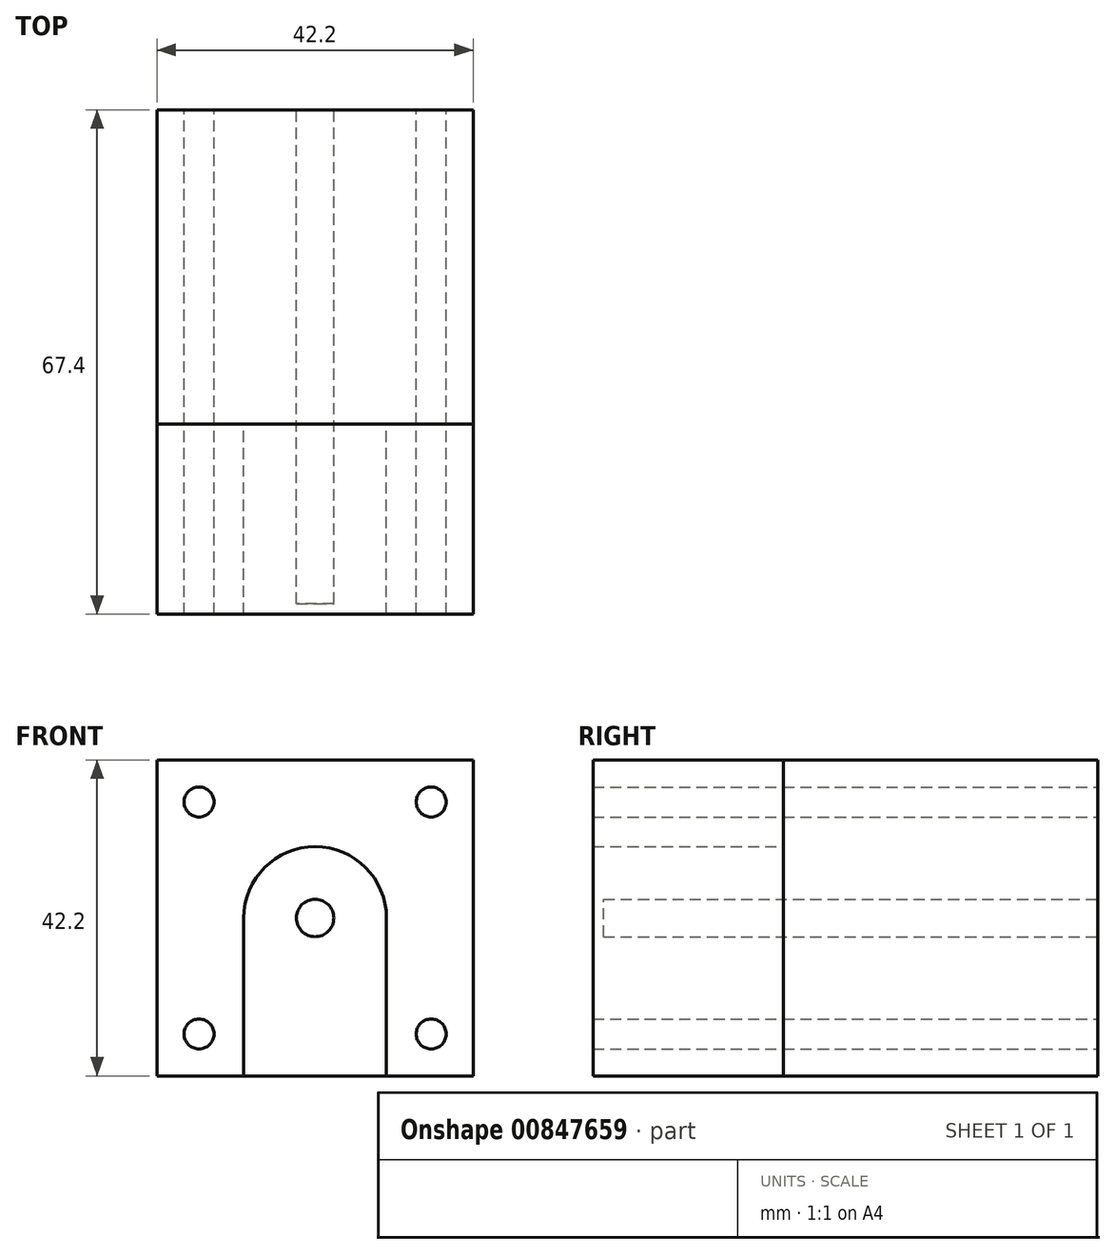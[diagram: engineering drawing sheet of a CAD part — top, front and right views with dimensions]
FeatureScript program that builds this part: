
annotation { "Feature Type Name" : "Feature", "Feature Type Description" : "" }
export const myFeature = defineFeature(function(context is Context, id is Id, definition is map)
    precondition{}
    {
        {
            var Q0;
            Q0=qCreatedBy(makeId("Front.planeOp"),FACE);
            var sketch = newSketch(context, id + "F0", { "sketchPlane" : qUnion([Q0])});
            skCircle(sketch, "E0", {"center": v(0, 0) * mm, "radius": 2.5 * mm});
            skCircle(sketch, "E1", {"center": v(0, 0) * mm, "radius": 11 * mm, "construction": true});
            skLineSegment(sketch, "E2.bottom", {"start": v(21.1, -21.1) * mm, "end": v(-21.1, -21.1) * mm});
            skLineSegment(sketch, "E2.top", {"start": v(21.1, 21.1) * mm, "end": v(-21.1, 21.1) * mm});
            skLineSegment(sketch, "E2.left", {"start": v(21.1, -21.1) * mm, "end": v(21.1, 21.1) * mm});
            skLineSegment(sketch, "E2.right", {"start": v(-21.1, -21.1) * mm, "end": v(-21.1, 21.1) * mm});
            skCircle(sketch, "E3", {"center": v(-15.5, 15.5) * mm, "radius": 2 * mm});
            skLineSegment(sketch, "E4", {"start": v(0, 21.1) * mm, "end": v(0, -21.1) * mm, "construction": true});
            skLineSegment(sketch, "E5", {"start": v(-21.1, 0) * mm, "end": v(21.1, 0) * mm, "construction": true});
            skCircle(sketch, "E6", {"center": v(15.5, 15.5) * mm, "radius": 2 * mm});
            skCircle(sketch, "E7", {"center": v(15.5, -15.5) * mm, "radius": 2 * mm});
            skCircle(sketch, "E8", {"center": v(-15.5, -15.5) * mm, "radius": 2 * mm});
            skSolve(sketch);
        }
        {
            var Q0;
            Q0=makeQuery(id+"F0.imprint","IMPRINT",FACE,{"disambiguationData":[TD([[makeQuery(id+"F0.imprint","IMPRINT",EDGE,{"derivedFrom":sQuery(id+"F0.wireOp",EDGE,"E0")}),-1.0]])]});
            var Q1;
            Q1=makeQuery(id+"F0.imprint","IMPRINT",FACE,{"disambiguationData":[TD([[makeQuery(id+"F0.imprint","IMPRINT",EDGE,{"derivedFrom":sQuery(id+"F0.wireOp",EDGE,"E0")}),1.0]])]});
            var Q2;
            Q2=sQuery(id+"F0.wireOp",EDGE,"E2.left");
            var Q3;
            Q3=sQuery(id+"F0.wireOp",EDGE,"E2.top");
            var Q4;
            Q4=sQuery(id+"F0.wireOp",EDGE,"E2.right");
            var Q5;
            Q5=sQuery(id+"F0.wireOp",EDGE,"E2.bottom");
            var Q6;
            Q6=sQuery(id+"F0.wireOp",EDGE,"E8");
            var Q7;
            Q7=sQuery(id+"F0.wireOp",EDGE,"E3");
            var Q8;
            Q8=sQuery(id+"F0.wireOp",EDGE,"E6");
            var Q9;
            Q9=sQuery(id+"F0.wireOp",EDGE,"E7");
            extrude(context, id + "F1", {"entities" : qUnion([Q0, Q1]), "surfaceEntities" : qUnion([Q2, Q3, Q4, Q5, Q6, Q7, Q8, Q9]), "depth" : 42 * mm, "offsetDistance" : 25.4 * mm});
        }
        {
            var Q0;
            Q0=makeQuery(id+"F0.imprint","IMPRINT",FACE,{"disambiguationData":[TD([[makeQuery(id+"F0.imprint","IMPRINT",EDGE,{"derivedFrom":sQuery(id+"F0.wireOp",EDGE,"E0")}),1.0]])]});
            var Q1;
            Q1=sQuery(id+"F0.wireOp",EDGE,"E0");
            extrude(context, id + "F2", {"entities" : qUnion([Q0]), "surfaceEntities" : qUnion([Q1]), "depth" : 66 * mm, "offsetDistance" : 25.4 * mm});
        }
        {
            var Q0;
            Q0=makeQuery(id+"F1.opExtrude","CAP_FACE",FACE,{"disambiguationData":[OSD([sQuery(id+"F0.wireOp",EDGE,"E2.bottom"),sQuery(id+"F0.wireOp",EDGE,"E2.top"),sQuery(id+"F0.wireOp",EDGE,"E2.left"),sQuery(id+"F0.wireOp",EDGE,"E2.right"),sQuery(id+"F0.wireOp",EDGE,"E3"),sQuery(id+"F0.wireOp",EDGE,"E6"),sQuery(id+"F0.wireOp",EDGE,"E7"),sQuery(id+"F0.wireOp",EDGE,"E8")])],"isStart":false});
            var sketch = newSketch(context, id + "F3", { "sketchPlane" : qUnion([Q0])});
            skArc(sketch, "E9", {"start": v(9.53, 0) * mm, "mid": v(0, 9.53) * mm, "end": v(-9.53, 0) * mm});
            skCircle(sketch, "E10", {"center": v(0, 0) * mm, "radius": 11 * mm, "construction": true});
            skLineSegment(sketch, "E11.bottom", {"start": v(21.1, -21.1) * mm, "end": v(9.53, -21.1) * mm});
            skLineSegment(sketch, "E11.top", {"start": v(21.1, 21.1) * mm, "end": v(-21.1, 21.1) * mm});
            skLineSegment(sketch, "E11.left", {"start": v(21.1, -21.1) * mm, "end": v(21.1, 21.1) * mm});
            skLineSegment(sketch, "E11.right", {"start": v(-21.1, -21.1) * mm, "end": v(-21.1, 21.1) * mm});
            skCircle(sketch, "E12", {"center": v(-15.5, 15.5) * mm, "radius": 2 * mm});
            skLineSegment(sketch, "E13", {"start": v(0, 21.1) * mm, "end": v(0, -21.1) * mm, "construction": true});
            skLineSegment(sketch, "E14", {"start": v(-21.1, 0) * mm, "end": v(21.1, 0) * mm, "construction": true});
            skCircle(sketch, "E15", {"center": v(15.5, 15.5) * mm, "radius": 2 * mm});
            skCircle(sketch, "E16", {"center": v(15.5, -15.5) * mm, "radius": 2 * mm});
            skCircle(sketch, "E17", {"center": v(-15.5, -15.5) * mm, "radius": 2 * mm});
            skLineSegment(sketch, "E18", {"start": v(-9.53, 0) * mm, "end": v(-9.52, -21.1) * mm});
            skLineSegment(sketch, "E19", {"start": v(9.53, 0) * mm, "end": v(9.53, -21.1) * mm});
            skLineSegment(sketch, "E20.trimOffspring", {"start": v(-9.52, -21.1) * mm, "end": v(-21.1, -21.1) * mm});
            skSolve(sketch);
        }
        {
            var Q0;
            Q0 = qSketchRegion(id + "F3", true);
            extrude(context, id + "F4", {"entities" : qUnion([Q0]), "depth" : 25.4 * mm, "offsetDistance" : 25.4 * mm});
        }
    });
